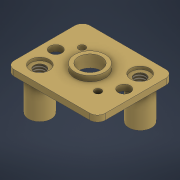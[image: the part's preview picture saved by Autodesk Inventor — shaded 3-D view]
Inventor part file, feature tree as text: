
AUTODESK INVENTOR PART (.ipt)
format: ipt  version: 2021 (Build 250183000, 183)  size: 205,824 bytes
history: native  units: mm
features: extrude x9, sketch x7, other x3, thread x2, fillet x1
ambient origin geometry x8: Origin, YZ Plane, XZ Plane, XY Plane, X Axis, Y Axis, Z Axis, Center Point
bodies: Body1 (feature_tree)
feature tree (22):
  other  "Chapa Superior"
  other  "Sólido1"
  extrude  "Extrusão1"  Depth=10.0mm
  fillet  "Arredondamento1"  Radius=0.8mm
  sketch  "Esboço2"  dims[d4=1.0mm d5=4.0mm]
  extrude  "Extrusão2"  Depth=1.0mm
  extrude  "Extrusão3"  Depth=0.7mm TaperAngle=0.0deg
  extrude  "Extrusão4"  Depth=1.6mm
  extrude  "Extrusão5"  Depth=0.9mm
  sketch  "Esboço5"  dims[d12=0.8mm d13=0.0mm d14=0.9mm]
  extrude  "Extrusão6"  Depth=0.8mm TaperAngle=0.0deg
  extrude  "Extrusão7"  Depth=0.1mm
  extrude  "Extrusão8"  Depth=0.4mm TaperAngle=0.0deg
  thread  "Rosca1"  [1 undecoded]
  thread  "Rosca2"  [1 undecoded]
  extrude  "Extrusão9"  Depth=0.1mm
  sketch  "Esboço1"  dims[d0=12.0mm d1=10.0mm d2=0.8mm d3=0.0mm]
  sketch  "Esboço3"  dims[d6=3.0mm d7=0.7mm d8=0.0mm]
  sketch  "Esboço4"  dims[d9=0.8mm d10=0.0mm d11=1.6mm]
  sketch  "Esboço6"  dims[d15=0.9mm d16=0.8mm d17=0.0mm]
  sketch  "Esboço10"  dims[d18=2.5mm d19=2.5mm d20=0.4mm d21=0.0mm d22=1.5mm d24=10.0mm d25=0.0mm d26=3.0mm d27=3.0mm d28=4.6mm d29=0.0mm d30=1.5mm d31=5.0mm d32=0.0mm d33=5.0mm d34=0.0mm d35=0.1mm d36=0.0mm]
  other  "Contorno projetado4"
note: 2 required parameter values undecoded (feature->parameter linkage not recoverable at this tier; creation-order binding heuristic only, values carry confidence <= 0.55)
